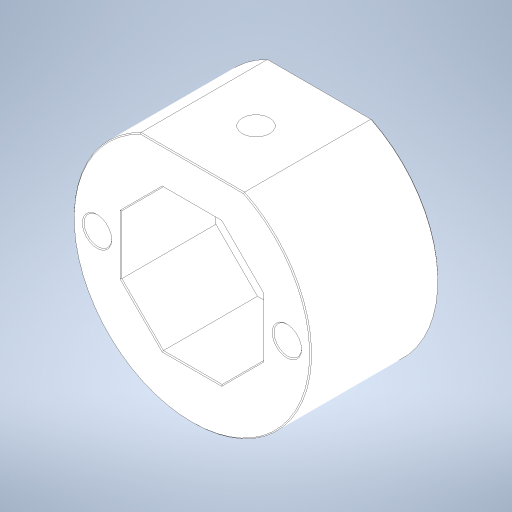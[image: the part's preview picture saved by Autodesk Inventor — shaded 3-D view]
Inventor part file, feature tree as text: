
AUTODESK INVENTOR PART (.ipt)
format: ipt  version: 2023 (Build 270158000, 158)  size: 327,680 bytes
history: native  units: mm
features: extrude x6, sketch x6, chamfer x4, projected_geometry x2
ambient origin geometry x8: Origin, YZ Plane, XZ Plane, XY Plane, X Axis, Y Axis, Z Axis, Center Point
bodies: Body1 (feature_tree)
feature tree (18):
  extrude  "Extrusion2"  Depth=22.5mm
  extrude  "Extrusion3"  Depth=5.75mm
  extrude  "Extrusion4"  Depth=21.794495mm
  extrude  "Extrusion6"  Depth=13.5mm
  extrude  "Extrusion7"  Depth=20.0mm TaperAngle=0.0deg
  extrude  "Extrusion8"  Depth=29.88mm
  chamfer  "Chamfer1"  Distance=20.0mm Angle=360.0deg
  chamfer  "Chamfer2"  Distance=7.0mm
  chamfer  "Chamfer3"  Distance=80.0mm Angle=360.0deg
  chamfer  "Chamfer4"  Distance=10.0mm
  sketch  "Sketch2"  dims[d4=50.0mm d5=22.5mm]
  sketch  "Sketch3"  dims[d6=27.0mm d7=0.0mm d8=5.75mm]
  sketch  "Sketch4"  dims[d9=10.897247mm d10=21.794495mm]
  sketch  "Sketch6"  dims[d11=27.0mm d12=13.5mm]
  projected_geometry  "Projected Loop2"
  sketch  "Sketch7"  dims[d13=15.0mm d14=0.0mm d15=20.0mm d16=0.0mm]
  sketch  "Sketch8"  dims[d20=40.0mm d21=5.8mm d22=20.0mm d24=360.0deg d26=7.0mm d27=0.0mm d28=80.0mm d30=360.0deg d32=10.0mm d33=0.0mm d34=6.0mm d35=0.0mm d36=0.0mm d37=0.2mm d38=2.0mm d39=45.0deg d40=0.2mm d41=2.0mm d42=45.0deg d43=0.2mm d44=2.0mm d45=45.0deg d47=29.88mm d48=14.94mm d49=14.94mm d50=29.88mm d51=0.2mm d52=2.0mm d53=45.0deg]
  projected_geometry  "Projected Loop3"
